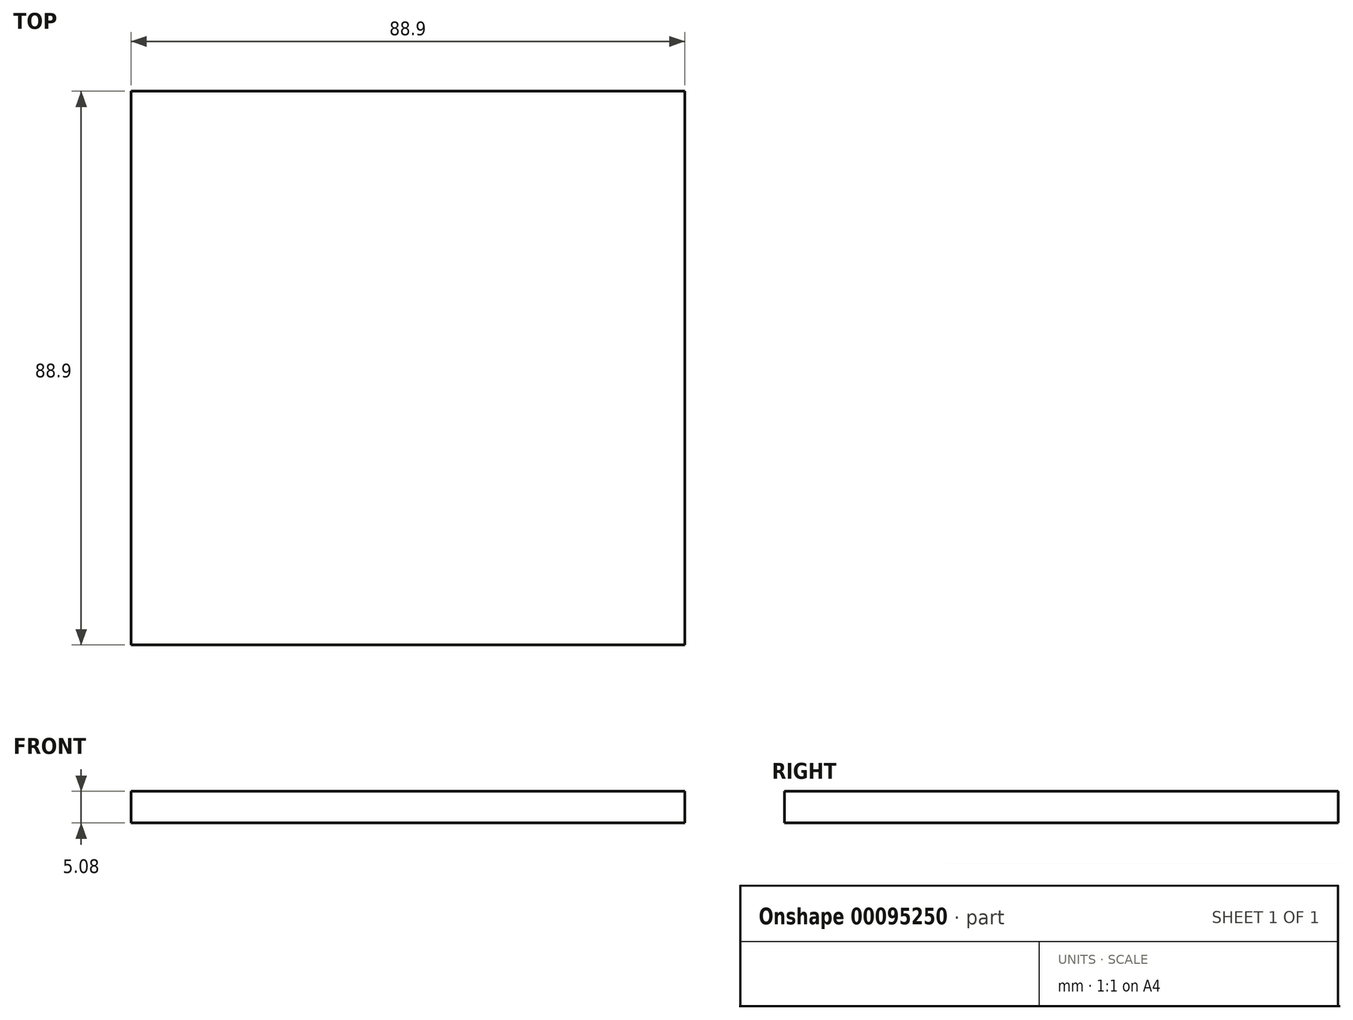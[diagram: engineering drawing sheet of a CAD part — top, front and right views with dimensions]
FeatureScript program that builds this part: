
annotation { "Feature Type Name" : "Feature", "Feature Type Description" : "" }
export const myFeature = defineFeature(function(context is Context, id is Id, definition is map)
    precondition{}
    {
        {
            var Q0;
            Q0=qCreatedBy(makeId("Top.planeOp"),FACE);
            var sketch = newSketch(context, id + "F0", { "sketchPlane" : qUnion([Q0])});
            skLineSegment(sketch, "E0.bottom", {"start": v(-39.96, 39.02) * mm, "end": v(48.94, 39.02) * mm});
            skLineSegment(sketch, "E0.top", {"start": v(-39.96, -49.88) * mm, "end": v(48.94, -49.88) * mm});
            skLineSegment(sketch, "E0.left", {"start": v(-39.96, 39.02) * mm, "end": v(-39.96, -49.88) * mm});
            skLineSegment(sketch, "E0.right", {"start": v(48.94, 39.02) * mm, "end": v(48.94, -49.88) * mm});
            skSolve(sketch);
        }
        {
            var Q0;
            Q0=makeQuery(id+"F0.imprint","IMPRINT",FACE,{"disambiguationData":[TD([[makeQuery(id+"F0.imprint","IMPRINT",EDGE,{"derivedFrom":sQuery(id+"F0.wireOp",EDGE,"E0.bottom")}),-1.0]])]});
            extrude(context, id + "F1", {"entities" : qUnion([Q0]), "depth" : 5.08 * mm});
        }
    });
